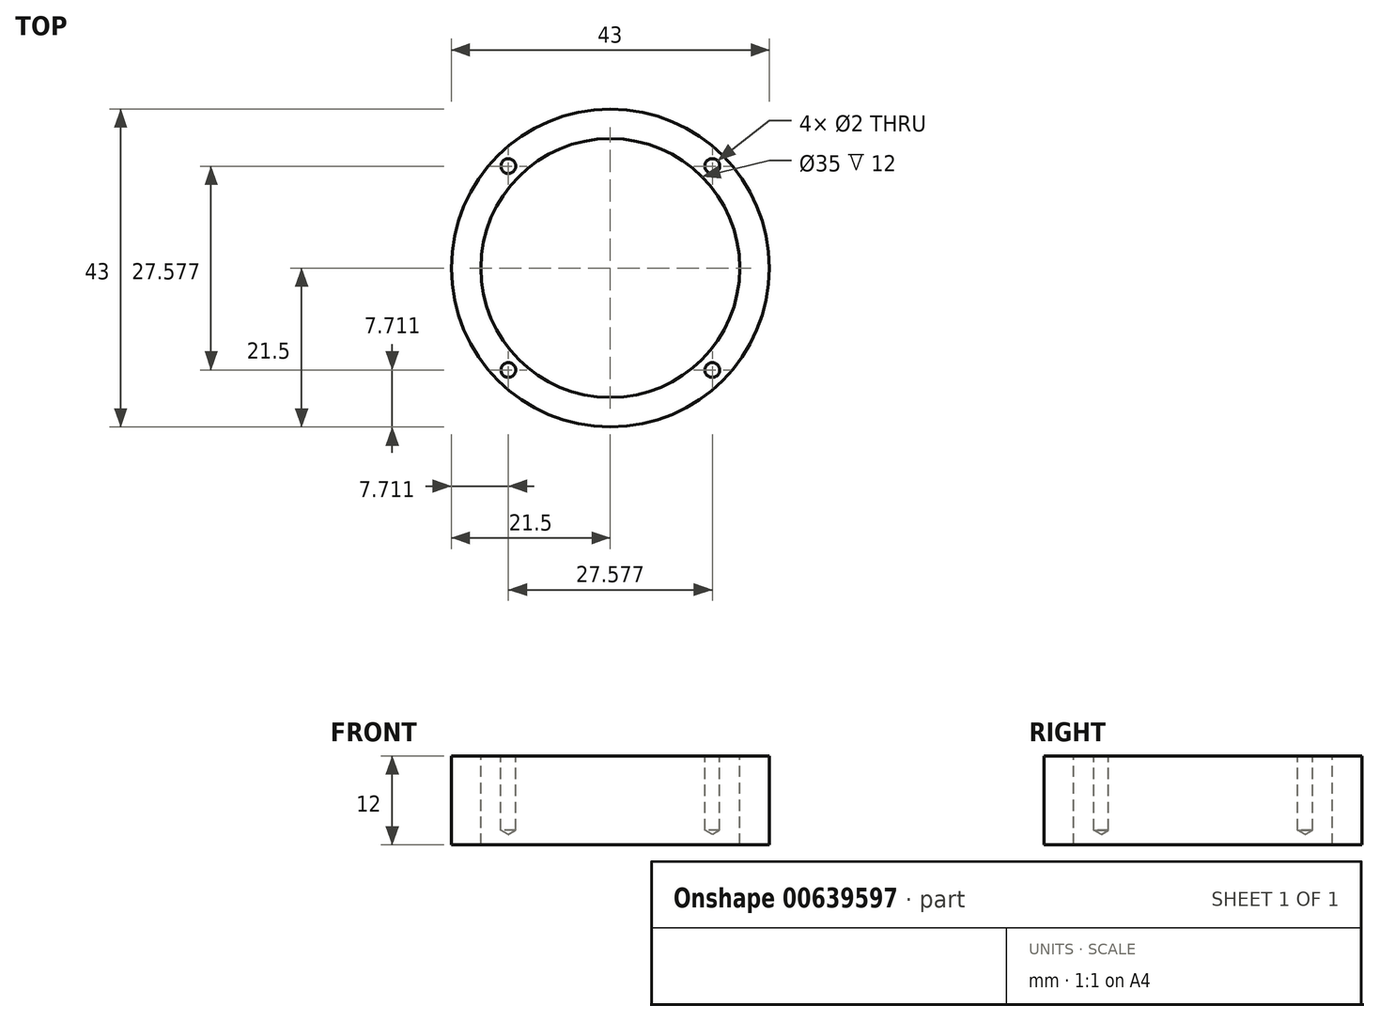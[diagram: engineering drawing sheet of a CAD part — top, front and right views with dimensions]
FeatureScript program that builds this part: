
annotation { "Feature Type Name" : "Feature", "Feature Type Description" : "" }
export const myFeature = defineFeature(function(context is Context, id is Id, definition is map)
    precondition{}
    {
        {
            var Q0;
            Q0=qCreatedBy(makeId("Top.planeOp"),FACE);
            var sketch = newSketch(context, id + "F0", { "sketchPlane" : qUnion([Q0])});
            skCircle(sketch, "E0", {"center": v(0, 0) * mm, "radius": 21.5 * mm});
            skSolve(sketch);
        }
        {
            var Q0;
            Q0=makeQuery(id+"F0.imprint","IMPRINT",FACE,{"disambiguationData":[TD([[makeQuery(id+"F0.imprint","IMPRINT",EDGE,{"derivedFrom":sQuery(id+"F0.wireOp",EDGE,"E0")}),1.0]])]});
            extrude(context, id + "F1", {"entities" : qUnion([Q0]), "depth" : 12 * mm, "offsetDistance" : 25 * mm});
        }
        {
            var Q0;
            Q0=makeQuery(id+"F1.opExtrude","CAP_FACE",FACE,{"disambiguationData":[OSD([sQuery(id+"F0.wireOp",EDGE,"E0")])],"isStart":false});
            var sketch = newSketch(context, id + "F2", { "sketchPlane" : qUnion([Q0])});
            skPoint(sketch, "E1", {"position": v(0, 0) * mm});
            skSolve(sketch);
        }
        {
            var Q0;
            Q0=sQuery(id+"F2.wireOp",VERTEX,"E1");
            var Q1;
            Q1=makeQuery(id+"F1.opExtrude","SWEPT_BODY",BODY,{"disambiguationData":[OSD([sQuery(id+"F0.wireOp",EDGE,"E0")])]});
            hole(context, id + "F3", {"style" : HoleStyle.SIMPLE, "endStyle" : HoleEndStyle.THROUGH, "holeDiameter" : 35 * mm, "majorDiameter" : 5 * mm, "isTappedThrough" : true, "tappedDepth" : 12 * mm, "tapClearance" : 3, "locations" : qUnion([Q0]), "scope" : qUnion([Q1])});
        }
        {
            var Q0;
            Q0=makeQuery(id+"F1.opExtrude","CAP_FACE",FACE,{"disambiguationData":[OSD([sQuery(id+"F0.wireOp",EDGE,"E0")])],"isStart":false});
            var sketch = newSketch(context, id + "F4", { "sketchPlane" : qUnion([Q0])});
            skPoint(sketch, "E2", {"position": v(-13.79, 13.79) * mm});
            skPoint(sketch, "E3", {"position": v(-13.79, -13.79) * mm});
            skPoint(sketch, "E4", {"position": v(13.79, -13.79) * mm});
            skPoint(sketch, "E5", {"position": v(13.79, 13.79) * mm});
            skLineSegment(sketch, "E6", {"start": v(0, 0) * mm, "end": v(-13.79, 13.79) * mm, "construction": true});
            skLineSegment(sketch, "E7", {"start": v(-13.79, -13.79) * mm, "end": v(0, 0) * mm, "construction": true});
            skLineSegment(sketch, "E8", {"start": v(0, 0) * mm, "end": v(13.79, 13.79) * mm, "construction": true});
            skLineSegment(sketch, "E9", {"start": v(13.79, -13.79) * mm, "end": v(0, 0) * mm, "construction": true});
            skSolve(sketch);
        }
        {
            var Q0;
            Q0=sQuery(id+"F4.wireOp",VERTEX,"E6.end");
            var Q1;
            Q1=sQuery(id+"F4.wireOp",VERTEX,"E5");
            var Q2;
            Q2=sQuery(id+"F4.wireOp",VERTEX,"E9.start");
            var Q3;
            Q3=sQuery(id+"F4.wireOp",VERTEX,"E3");
            var Q4;
            Q4=makeQuery(id+"F1.opExtrude","SWEPT_BODY",BODY,{"disambiguationData":[OSD([sQuery(id+"F0.wireOp",EDGE,"E0")])]});
            hole(context, id + "F5", {"style" : HoleStyle.SIMPLE, "endStyle" : HoleEndStyle.BLIND, "holeDiameter" : 2 * mm, "majorDiameter" : 5 * mm, "holeDepth" : 10 * mm, "isTappedThrough" : true, "tappedDepth" : 12 * mm, "tapClearance" : 3, "locations" : qUnion([Q0, Q1, Q2, Q3]), "scope" : qUnion([Q4])});
        }
    });
